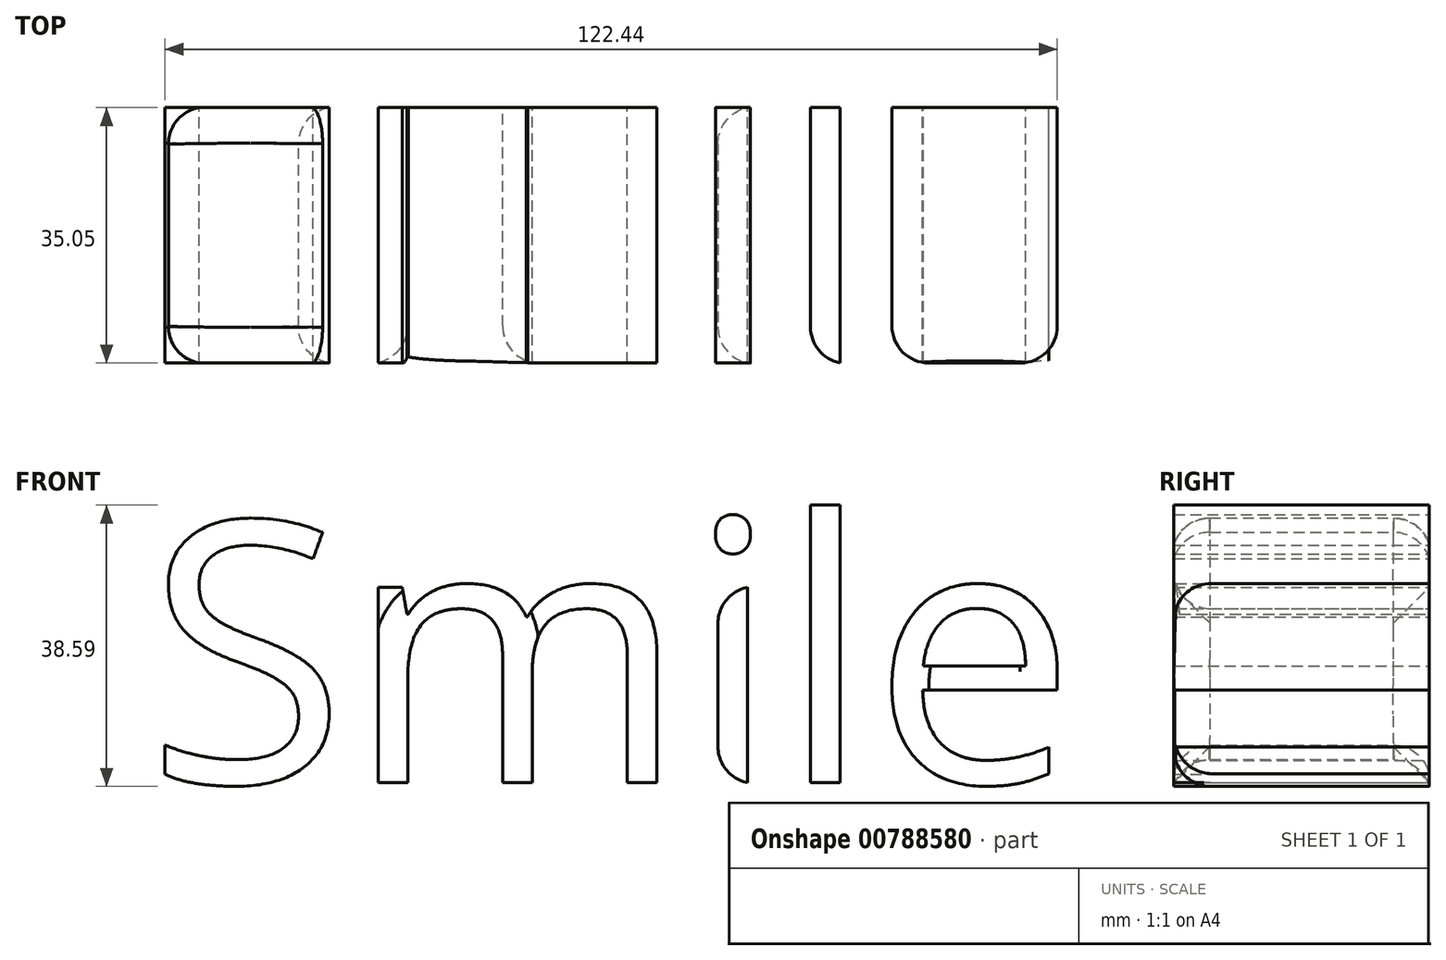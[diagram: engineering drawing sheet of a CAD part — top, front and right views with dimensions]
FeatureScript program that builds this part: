
annotation { "Feature Type Name" : "Feature", "Feature Type Description" : "" }
export const myFeature = defineFeature(function(context is Context, id is Id, definition is map)
    precondition{}
    {
        {
            var Q0;
            Q0=qCreatedBy(makeId("Front.planeOp"),FACE);
            var sketch = newSketch(context, id + "F0", { "sketchPlane" : qUnion([Q0])});
            skArc(sketch, "E0", {"start": v(-37.67, -41.53) * mm, "mid": v(-1.54, -71.14) * mm, "end": v(35.65, -42.87) * mm});
            skLineSegment(sketch, "E1", {"start": v(-18.39, -8.3) * mm, "end": v(-18.39, -14.99) * mm});
            skLineSegment(sketch, "E2", {"start": v(13.31, -8.88) * mm, "end": v(13.31, -15.75) * mm});
            skText(sketch, "E3", { "text": "Smile\n", "fontName": "OpenSans-Regular.ttf"});
            const initialGuessF0  = {"E3": [-0.06479, 0.0297, 1, 0, 0.0361]};
            skSetInitialGuess(sketch, initialGuessF0);
            skSolve(sketch);
        }
        {
            var Q0;
            Q0 = qSketchRegion(id + "F0", true);
            extrude(context, id + "F1", {"entities" : qUnion([Q0]), "depth" : 35.05 * mm, "offsetDistance" : 25.4 * mm});
        }
        {
            var Q0;
            Q0=makeQuery(id+"F1.opExtrude","CAP_EDGE",EDGE,{"disambiguationData":[OSD([sQuery(id+"F0.wireOp",EDGE,"E3.sketch_text.stroke-14")])],"isStart":false});
            var Q1;
            Q1=makeQuery(id+"F1.opExtrude","CAP_EDGE",EDGE,{"disambiguationData":[OSD([sQuery(id+"F0.wireOp",EDGE,"E3.sketch_text.stroke-15")])],"isStart":false});
            var Q2;
            Q2=makeQuery(id+"F1.opExtrude","CAP_EDGE",EDGE,{"disambiguationData":[OSD([sQuery(id+"F0.wireOp",EDGE,"E3.sketch_text.stroke-13")])],"isStart":false});
            var Q3;
            Q3=makeQuery(id+"F1.opExtrude","CAP_EDGE",EDGE,{"disambiguationData":[OSD([sQuery(id+"F0.wireOp",EDGE,"E3.sketch_text.stroke-12")])],"isStart":false});
            var Q4;
            Q4=makeQuery(id+"F1.opExtrude","CAP_EDGE",EDGE,{"disambiguationData":[OSD([sQuery(id+"F0.wireOp",EDGE,"E3.sketch_text.stroke-10")])],"isStart":false});
            var Q5;
            Q5=makeQuery(id+"F1.opExtrude","CAP_EDGE",EDGE,{"disambiguationData":[OSD([sQuery(id+"F0.wireOp",EDGE,"E3.sketch_text.stroke-9")])],"isStart":false});
            var Q6;
            Q6=makeQuery(id+"F1.opExtrude","CAP_EDGE",EDGE,{"disambiguationData":[OSD([sQuery(id+"F0.wireOp",EDGE,"E3.sketch_text.stroke-8")])],"isStart":false});
            var Q7;
            Q7=makeQuery(id+"F1.opExtrude","CAP_EDGE",EDGE,{"disambiguationData":[OSD([sQuery(id+"F0.wireOp",EDGE,"E3.sketch_text.stroke-7")])],"isStart":false});
            var Q8;
            Q8=makeQuery(id+"F1.opExtrude","CAP_EDGE",EDGE,{"disambiguationData":[OSD([sQuery(id+"F0.wireOp",EDGE,"E3.sketch_text.stroke-6")])],"isStart":false});
            var Q9;
            Q9=makeQuery(id+"F1.opExtrude","CAP_EDGE",EDGE,{"disambiguationData":[OSD([sQuery(id+"F0.wireOp",EDGE,"E3.sketch_text.stroke-5")])],"isStart":false});
            var Q10;
            Q10=makeQuery(id+"F1.opExtrude","CAP_EDGE",EDGE,{"disambiguationData":[OSD([sQuery(id+"F0.wireOp",EDGE,"E3.sketch_text.stroke-4")])],"isStart":false});
            var Q11;
            Q11=makeQuery(id+"F1.opExtrude","CAP_EDGE",EDGE,{"disambiguationData":[OSD([sQuery(id+"F0.wireOp",EDGE,"E3.sketch_text.stroke-11")])],"isStart":false});
            fillet(context, id + "F2", {"entities" : qUnion([Q0, Q1, Q2, Q3, Q4, Q5, Q6, Q7, Q8, Q9, Q10, Q11]), "radius" : 5.08 * mm, "tangentPropagation" : true, "allowEdgeOverflow" : false});
        }
        {
            var Q0;
            Q0=makeQuery(id+"F1.opExtrude","CAP_EDGE",EDGE,{"disambiguationData":[OSD([sQuery(id+"F0.wireOp",EDGE,"E3.sketch_text.stroke-15")])],"isStart":true});
            var Q1;
            Q1=makeQuery(id+"F1.opExtrude","CAP_EDGE",EDGE,{"disambiguationData":[OSD([sQuery(id+"F0.wireOp",EDGE,"E3.sketch_text.stroke-14")])],"isStart":true});
            var Q2;
            Q2=makeQuery(id+"F1.opExtrude","CAP_EDGE",EDGE,{"disambiguationData":[OSD([sQuery(id+"F0.wireOp",EDGE,"E3.sketch_text.stroke-13")])],"isStart":true});
            var Q3;
            Q3=makeQuery(id+"F1.opExtrude","CAP_EDGE",EDGE,{"disambiguationData":[OSD([sQuery(id+"F0.wireOp",EDGE,"E3.sketch_text.stroke-12")])],"isStart":true});
            var Q4;
            Q4=makeQuery(id+"F1.opExtrude","CAP_EDGE",EDGE,{"disambiguationData":[OSD([sQuery(id+"F0.wireOp",EDGE,"E3.sketch_text.stroke-11")])],"isStart":true});
            var Q5;
            Q5=makeQuery(id+"F1.opExtrude","CAP_EDGE",EDGE,{"disambiguationData":[OSD([sQuery(id+"F0.wireOp",EDGE,"E3.sketch_text.stroke-10")])],"isStart":true});
            var Q6;
            Q6=makeQuery(id+"F1.opExtrude","CAP_EDGE",EDGE,{"disambiguationData":[OSD([sQuery(id+"F0.wireOp",EDGE,"E3.sketch_text.stroke-9")])],"isStart":true});
            var Q7;
            Q7=makeQuery(id+"F1.opExtrude","CAP_EDGE",EDGE,{"disambiguationData":[OSD([sQuery(id+"F0.wireOp",EDGE,"E3.sketch_text.stroke-8")])],"isStart":true});
            var Q8;
            Q8=makeQuery(id+"F1.opExtrude","CAP_EDGE",EDGE,{"disambiguationData":[OSD([sQuery(id+"F0.wireOp",EDGE,"E3.sketch_text.stroke-7")])],"isStart":true});
            var Q9;
            Q9=makeQuery(id+"F1.opExtrude","CAP_EDGE",EDGE,{"disambiguationData":[OSD([sQuery(id+"F0.wireOp",EDGE,"E3.sketch_text.stroke-6")])],"isStart":true});
            var Q10;
            Q10=makeQuery(id+"F1.opExtrude","CAP_EDGE",EDGE,{"disambiguationData":[OSD([sQuery(id+"F0.wireOp",EDGE,"E3.sketch_text.stroke-5")])],"isStart":true});
            var Q11;
            Q11=makeQuery(id+"F1.opExtrude","CAP_EDGE",EDGE,{"disambiguationData":[OSD([sQuery(id+"F0.wireOp",EDGE,"E3.sketch_text.stroke-4")])],"isStart":true});
            fillet(context, id + "F3", {"entities" : qUnion([Q0, Q1, Q2, Q3, Q4, Q5, Q6, Q7, Q8, Q9, Q10, Q11]), "radius" : 5.08 * mm, "tangentPropagation" : true, "allowEdgeOverflow" : false});
        }
        {
            var Q0;
            Q0=makeQuery(id+"F1.opExtrude","CAP_EDGE",EDGE,{"disambiguationData":[OSD([sQuery(id+"F0.wireOp",EDGE,"E3.sketch_text.stroke-37")])],"isStart":false});
            var Q1;
            Q1=makeQuery(id+"F1.opExtrude","CAP_EDGE",EDGE,{"disambiguationData":[OSD([sQuery(id+"F0.wireOp",EDGE,"E3.sketch_text.stroke-36")])],"isStart":false});
            var Q2;
            Q2=makeQuery(id+"F1.opExtrude","CAP_EDGE",EDGE,{"disambiguationData":[OSD([sQuery(id+"F0.wireOp",EDGE,"E3.sketch_text.stroke-34")])],"isStart":false});
            var Q3;
            Q3=makeQuery(id+"F1.opExtrude","CAP_EDGE",EDGE,{"disambiguationData":[OSD([sQuery(id+"F0.wireOp",EDGE,"E3.sketch_text.stroke-35")])],"isStart":false});
            fillet(context, id + "F4", {"entities" : qUnion([Q0, Q1, Q2, Q3]), "radius" : 5.08 * mm, "tangentPropagation" : true, "allowEdgeOverflow" : false});
        }
        {
            var Q0;
            Q0=makeQuery(id+"F1.opExtrude","SWEPT_FACE",FACE,{"disambiguationData":[OSD([sQuery(id+"F0.wireOp",EDGE,"E3.sketch_text.stroke-54")])]});
            fillet(context, id + "F5", {"entities" : qUnion([Q0]), "radius" : 5.08 * mm, "tangentPropagation" : true, "allowEdgeOverflow" : false});
        }
        {
            var Q0;
            Q0=makeQuery(id+"F1.opExtrude","CAP_EDGE",EDGE,{"disambiguationData":[OSD([sQuery(id+"F0.wireOp",EDGE,"E3.sketch_text.stroke-66")])],"isStart":false});
            fillet(context, id + "F6", {"entities" : qUnion([Q0]), "radius" : 5.08 * mm, "tangentPropagation" : true, "allowEdgeOverflow" : false});
        }
        {
            var Q0;
            Q0=makeQuery(id+"F1.opExtrude","CAP_EDGE",EDGE,{"disambiguationData":[OSD([sQuery(id+"F0.wireOp",EDGE,"E3.sketch_text.stroke-81")])],"isStart":false});
            var Q1;
            Q1=makeQuery(id+"F1.opExtrude","CAP_EDGE",EDGE,{"disambiguationData":[OSD([sQuery(id+"F0.wireOp",EDGE,"E3.sketch_text.stroke-82")])],"isStart":false});
            var Q2;
            Q2=makeQuery(id+"F1.opExtrude","CAP_EDGE",EDGE,{"disambiguationData":[OSD([sQuery(id+"F0.wireOp",EDGE,"E3.sketch_text.stroke-69")])],"isStart":false});
            var Q3;
            Q3=makeQuery(id+"F1.opExtrude","CAP_EDGE",EDGE,{"disambiguationData":[OSD([sQuery(id+"F0.wireOp",EDGE,"E3.sketch_text.stroke-70")])],"isStart":false});
            var Q4;
            Q4=makeQuery(id+"F1.opExtrude","CAP_EDGE",EDGE,{"disambiguationData":[OSD([sQuery(id+"F0.wireOp",EDGE,"E3.sketch_text.stroke-71")])],"isStart":false});
            var Q5;
            Q5=makeQuery(id+"F1.opExtrude","CAP_EDGE",EDGE,{"disambiguationData":[OSD([sQuery(id+"F0.wireOp",EDGE,"E3.sketch_text.stroke-72")])],"isStart":false});
            var Q6;
            Q6=makeQuery(id+"F1.opExtrude","CAP_EDGE",EDGE,{"disambiguationData":[OSD([sQuery(id+"F0.wireOp",EDGE,"E3.sketch_text.stroke-73")])],"isStart":false});
            var Q7;
            Q7=makeQuery(id+"F1.opExtrude","CAP_EDGE",EDGE,{"disambiguationData":[OSD([sQuery(id+"F0.wireOp",EDGE,"E3.sketch_text.stroke-74")])],"isStart":false});
            var Q8;
            Q8=makeQuery(id+"F1.opExtrude","CAP_EDGE",EDGE,{"disambiguationData":[OSD([sQuery(id+"F0.wireOp",EDGE,"E3.sketch_text.stroke-75")])],"isStart":false});
            fillet(context, id + "F7", {"entities" : qUnion([Q0, Q1, Q2, Q3, Q4, Q5, Q6, Q7, Q8]), "radius" : 5.08 * mm, "tangentPropagation" : true, "allowEdgeOverflow" : false});
        }
    });
